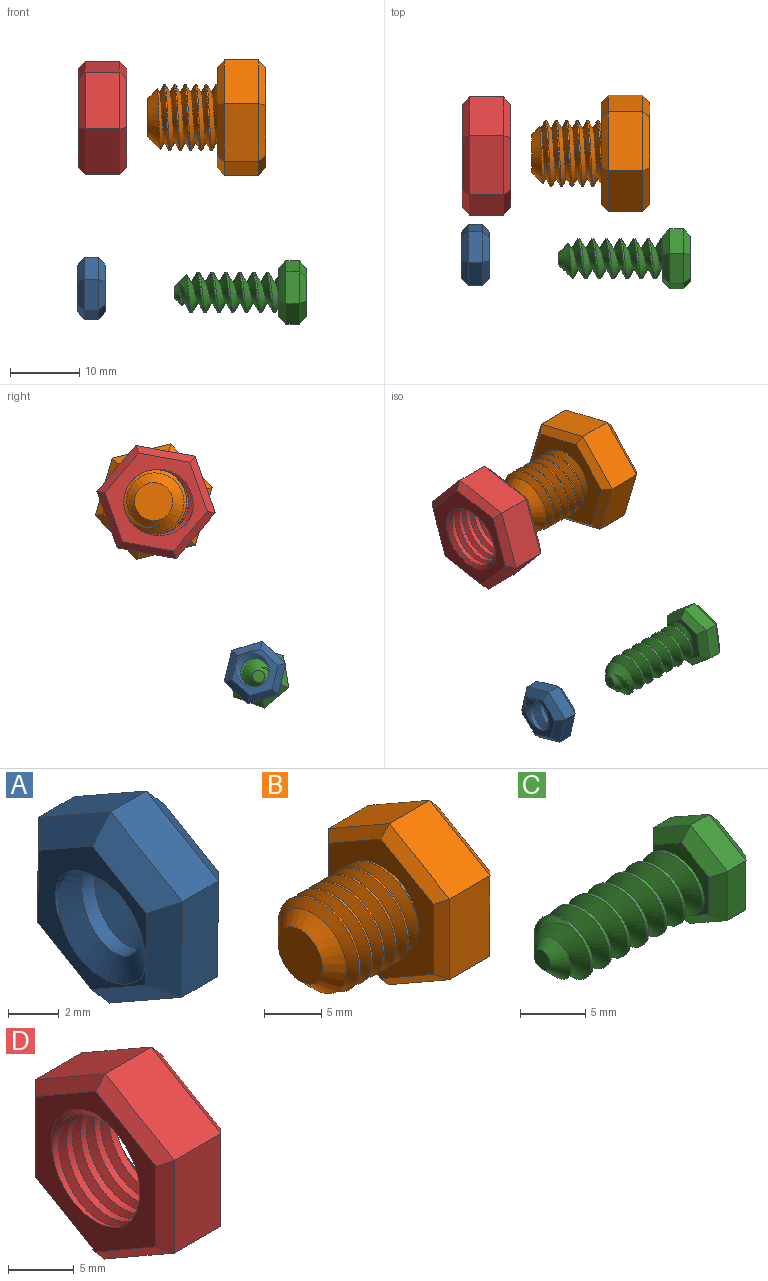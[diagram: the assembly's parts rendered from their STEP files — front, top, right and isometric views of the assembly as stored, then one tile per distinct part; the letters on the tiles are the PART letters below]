
ASSEMBLY  parts=4 mates=2
PART A: 23 faces, bbox 5.9x8.6x9.8 mm
  f0: cylinder r=2.04mm len=4.08mm, axis (1,0,0), area 18mm2, adj f7,f8,f21,f22
  f1: plane 3.98x2.34mm, normal (0,-0.51,0.86), area 9.2mm2, adj f2,f6,f14,f18
  f2: plane 4.62x2mm, normal (0,-1,-0.01), area 9.2mm2, adj f1,f3,f12,f16
  f3: plane 4.02x2.28mm, normal (0,-0.49,-0.87), area 9.2mm2, adj f2,f4,f10,f15
  f4: plane 3.98x2.34mm, normal (0,0.51,-0.86), area 9.2mm2, adj f3,f5,f9,f17
  f5: plane 4.62x2mm, normal (0,1,0.01), area 9.2mm2, adj f4,f6,f11,f19
  f6: plane 4.02x2.28mm, normal (0,0.49,0.87), area 9.2mm2, adj f1,f5,f13,f20
  f7: plane 7.5x6.6mm, normal (-1,0,0), area 12.6mm2, adj f0,f9,f10,f11,f12,f13,f14,f21
  f8: plane 7.5x6.6mm, normal (1,0,0), area 12.6mm2, adj f0,f15,f16,f17,f18,f19,f20,f21
  f9: plane 3.99x2.91mm, normal (-0.71,0.36,-0.61), area 5.7mm2, adj f4,f7,f10,f11
  f10: plane 4.02x2.87mm, normal (-0.71,-0.35,-0.61), area 5.7mm2, adj f3,f7,f9,f12
  f11: plane 4.62x1.03mm, normal (-0.71,0.71,0.01), area 5.7mm2, adj f5,f7,f9,f13
  f12: plane 4.62x1.03mm, normal (-0.71,-0.71,-0.01), area 5.7mm2, adj f2,f7,f10,f14
  f13: plane 4.02x2.87mm, normal (-0.71,0.35,0.61), area 5.7mm2, adj f6,f7,f11,f14
  f14: plane 3.99x2.91mm, normal (-0.71,-0.36,0.61), area 5.7mm2, adj f1,f7,f12,f13
  f15: plane 4.02x2.87mm, normal (0.71,-0.35,-0.61), area 5.7mm2, adj f3,f8,f16,f17
  f16: plane 4.8x1.21mm, normal (0.71,-0.71,-0.01), area 5.7mm2, adj f2,f8,f15,f18,f21,f22
  f17: plane 3.99x2.91mm, normal (0.71,0.36,-0.61), area 5.7mm2, adj f4,f8,f15,f19
  f18: plane 3.99x2.91mm, normal (0.71,-0.36,0.61), area 5.7mm2, adj f1,f8,f16,f20
  f19: plane 4.62x1.03mm, normal (0.71,0.71,0.01), area 5.7mm2, adj f5,f8,f17,f20
  f20: plane 4.02x2.87mm, normal (0.71,0.35,0.61), area 5.7mm2, adj f6,f8,f18,f19
  f21: bspline ~6.31x6.3mm, area 42.7mm2, adj f0,f7,f8,f16,f22
  f22: bspline ~6.31x6.31mm, area 42.7mm2, adj f0,f7,f8,f16,f21
PART B: 25 faces, bbox 17.8x15.9x18.1 mm
  f0: cylinder r=4.75mm len=9.5mm, axis (1,0,0), area 28.1mm2, adj f1,f2,f4,f12
  f1: bspline ~10.97x9.91mm, area 196.7mm2, adj f0,f2,f4,f12
  f2: bspline ~10.97x10.66mm, area 196.6mm2, adj f0,f1,f4,f12
  f3: plane 5.5x5.5mm, normal (-1,0,0), area 23.8mm2, adj f4
  f4: cone r=4.75mm half-angle=45deg, axis (1,0,0), area 47.4mm2, adj f0,f1,f2,f3
  f5: plane 7.48x5mm, normal (0,-0.5,0.86), area 43.3mm2, adj f6,f10,f18,f22
  f6: plane 8.66x5mm, normal (0,-1,0), area 43.3mm2, adj f5,f7,f16,f20
  f7: plane 7.52x5mm, normal (0,-0.5,-0.87), area 43.3mm2, adj f6,f8,f14,f19
  f8: plane 7.48x5mm, normal (0,0.5,-0.86), area 43.3mm2, adj f7,f9,f13,f21
  f9: plane 8.66x5mm, normal (0,1,0), area 43.3mm2, adj f8,f10,f15,f23
  f10: plane 7.52x5mm, normal (0,0.5,0.87), area 43.3mm2, adj f5,f9,f17,f24
  f11: plane 15.01x13.03mm, normal (1,0,0), area 146.4mm2, adj f13,f14,f15,f16,f17,f18
  f12: plane 15.83x13.85mm, normal (-1,0,0), area 89.2mm2, adj f0,f1,f2,f19,f20,f21,f22,f23
  f13: plane 7.49x4.93mm, normal (0.71,0.36,-0.61), area 11.4mm2, adj f8,f11,f14,f15
  f14: plane 7.52x4.88mm, normal (0.71,-0.35,-0.61), area 11.4mm2, adj f7,f11,f13,f16
  f15: plane 8.66x1.03mm, normal (0.71,0.71,0), area 11.4mm2, adj f9,f11,f13,f17
  f16: plane 8.66x1.03mm, normal (0.71,-0.71,0), area 11.4mm2, adj f6,f11,f14,f18
  f17: plane 7.52x4.88mm, normal (0.71,0.35,0.61), area 11.4mm2, adj f10,f11,f15,f18
  f18: plane 7.49x4.93mm, normal (0.71,-0.36,0.61), area 11.4mm2, adj f5,f11,f16,f17
  f19: plane 7.52x4.88mm, normal (-0.71,-0.35,-0.61), area 11.4mm2, adj f7,f12,f20,f21
  f20: plane 8.66x1.03mm, normal (-0.71,-0.71,0), area 11.4mm2, adj f6,f12,f19,f22
  f21: plane 7.49x4.93mm, normal (-0.71,0.36,-0.61), area 11.4mm2, adj f8,f12,f19,f23
  f22: plane 7.49x4.93mm, normal (-0.71,-0.36,0.61), area 11.4mm2, adj f5,f12,f20,f24
  f23: plane 8.66x1.03mm, normal (-0.71,0.71,0), area 11.4mm2, adj f9,f12,f21,f24
  f24: plane 7.52x4.88mm, normal (-0.71,0.35,0.61), area 11.4mm2, adj f10,f12,f22,f23
PART C: 25 faces, bbox 20.6x9.1x10.3 mm
  f0: cylinder r=2.88mm len=13mm, axis (1,0,0), area 35mm2, adj f1,f2,f4,f12
  f1: bspline ~15.88x6.65mm, area 161.3mm2, adj f0,f2,f4,f12
  f2: bspline ~16.54x6.65mm, area 160.1mm2, adj f0,f1,f4,f12
  f3: plane 1.76x1.76mm, normal (-1,0,0), area 2.4mm2, adj f4
  f4: cone r=2.88mm half-angle=45deg, axis (1,0,0), area 19.4mm2, adj f0,f1,f2,f3
  f5: plane 3.98x2.34mm, normal (0,-0.51,0.86), area 9.2mm2, adj f6,f10,f18,f22
  f6: plane 4.62x2mm, normal (0,-1,-0.01), area 9.2mm2, adj f5,f7,f16,f20
  f7: plane 4.02x2.28mm, normal (0,-0.49,-0.87), area 9.2mm2, adj f6,f8,f14,f19
  f8: plane 3.98x2.34mm, normal (0,0.51,-0.86), area 9.2mm2, adj f7,f9,f13,f21
  f9: plane 4.62x2mm, normal (0,1,0.01), area 9.2mm2, adj f8,f10,f15,f23
  f10: plane 4.02x2.28mm, normal (0,0.49,0.87), area 9.2mm2, adj f5,f9,f17,f24
  f11: plane 6.93x6.03mm, normal (1,0,0), area 31.2mm2, adj f13,f14,f15,f16,f17,f18
  f12: plane 7.96x7.06mm, normal (-1,0,0), area 15mm2, adj f0,f1,f2,f19,f20,f21,f22,f23
  f13: plane 3.99x2.91mm, normal (0.71,0.36,-0.61), area 5.7mm2, adj f8,f11,f14,f15
  f14: plane 4.02x2.86mm, normal (0.71,-0.35,-0.62), area 5.7mm2, adj f7,f11,f13,f16
  f15: plane 4.62x1.03mm, normal (0.71,0.71,0.01), area 5.7mm2, adj f9,f11,f13,f17
  f16: plane 4.62x1.03mm, normal (0.71,-0.71,-0.01), area 5.7mm2, adj f6,f11,f14,f18
  f17: plane 4.02x2.86mm, normal (0.71,0.35,0.62), area 5.7mm2, adj f10,f11,f15,f18
  f18: plane 3.99x2.91mm, normal (0.71,-0.36,0.61), area 5.7mm2, adj f5,f11,f16,f17
  f19: plane 4.02x2.86mm, normal (-0.71,-0.35,-0.62), area 5.7mm2, adj f7,f12,f20,f21
  f20: plane 4.62x1.03mm, normal (-0.71,-0.71,-0.01), area 5.7mm2, adj f6,f12,f19,f22
  f21: plane 3.99x2.91mm, normal (-0.71,0.36,-0.61), area 5.7mm2, adj f8,f12,f19,f23
  f22: plane 3.99x2.91mm, normal (-0.71,-0.36,0.61), area 5.7mm2, adj f5,f12,f20,f24
  f23: plane 4.62x1.03mm, normal (-0.71,0.71,0.01), area 5.7mm2, adj f9,f12,f21,f24
  f24: plane 4.02x2.86mm, normal (-0.71,0.35,0.62), area 5.7mm2, adj f10,f12,f22,f23
PART D: 23 faces, bbox 9.1x15.4x17.7 mm
  f0: plane 7.49x5mm, normal (0,-0.5,0.86), area 43.3mm2, adj f1,f5,f13,f17
  f1: plane 8.66x5mm, normal (0,-1,0), area 43.3mm2, adj f0,f2,f11,f15
  f2: plane 7.51x5mm, normal (0,-0.5,-0.87), area 43.3mm2, adj f1,f3,f9,f14
  f3: plane 7.49x5mm, normal (0,0.5,-0.86), area 43.3mm2, adj f2,f4,f8,f16
  f4: plane 8.66x5mm, normal (0,1,0), area 43.3mm2, adj f3,f5,f10,f18
  f5: plane 7.51x5mm, normal (0,0.5,0.87), area 43.3mm2, adj f0,f4,f12,f19
  f6: plane 15.37x13.38mm, normal (-1,0,0), area 71.4mm2, adj f8,f9,f10,f11,f12,f13,f20,f21
  f7: plane 15.37x13.38mm, normal (1,0,0), area 71.4mm2, adj f14,f15,f16,f17,f18,f19,f20,f21
  f8: plane 7.49x4.93mm, normal (-0.71,0.36,-0.61), area 11.4mm2, adj f3,f6,f9,f10
  f9: plane 7.51x4.89mm, normal (-0.71,-0.35,-0.61), area 11.4mm2, adj f2,f6,f8,f11
  f10: plane 8.66x1.02mm, normal (-0.71,0.71,0), area 11.4mm2, adj f4,f6,f8,f12
  f11: plane 8.66x1.02mm, normal (-0.71,-0.71,0), area 11.4mm2, adj f1,f6,f9,f13
  f12: plane 7.51x4.89mm, normal (-0.71,0.35,0.61), area 11.4mm2, adj f5,f6,f10,f13
  f13: plane 7.49x4.93mm, normal (-0.71,-0.36,0.61), area 11.4mm2, adj f0,f6,f11,f12
  f14: plane 7.51x4.89mm, normal (0.71,-0.35,-0.61), area 11.4mm2, adj f2,f7,f15,f16
  f15: plane 8.66x1.02mm, normal (0.71,-0.71,0), area 11.4mm2, adj f1,f7,f14,f17
  f16: plane 7.49x4.93mm, normal (0.71,0.36,-0.61), area 11.4mm2, adj f3,f7,f14,f18
  f17: plane 7.49x4.93mm, normal (0.71,-0.36,0.61), area 11.4mm2, adj f0,f7,f15,f19
  f18: plane 8.66x1.02mm, normal (0.71,0.71,0), area 11.4mm2, adj f4,f7,f16,f19
  f19: plane 7.51x4.89mm, normal (0.71,0.35,0.61), area 11.4mm2, adj f5,f7,f17,f18
  f20: cylinder r=4.66mm len=9.32mm, axis (1,0,0), area 85.4mm2, adj f6,f7,f21,f22
  f21: bspline ~12.5x10.82mm, area 128.4mm2, adj f6,f7,f20,f22
  f22: bspline ~12.5x10.82mm, area 128.5mm2, adj f6,f7,f20,f21
PLACE A rot(axis=(0,0.6,-0.8),180deg) t=(-55.27,-6.86,23.48)mm fixed
PLACE B rot(axis=(-1,0,0),43.8deg) t=(-31.66,7.73,48.08)mm
PLACE C rot(axis=(1,0,0),109.9deg) t=(-24.27,-7.4,22.91)mm
PLACE D rot(axis=(1,0,0),100.2deg) t=(-48.16,7.38,48.02)mm fixed
MATE cylindrical C.f0 <-> A.f7  axis (-1,0,0) through (-41.27,-7.4,22.91)mm
MATE cylindrical B.f0 <-> D.f6  axis (-1,0,0) through (-45.16,7.73,48.08)mm
